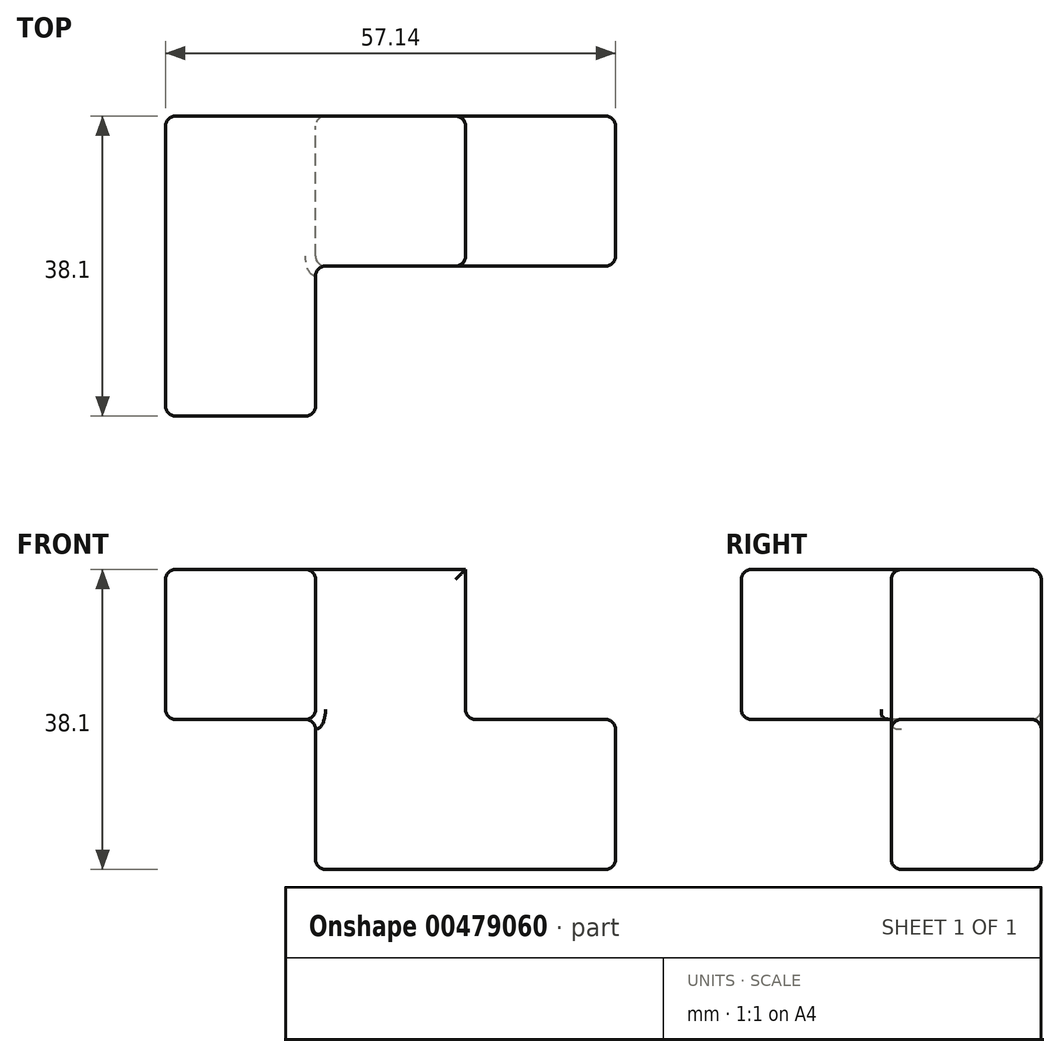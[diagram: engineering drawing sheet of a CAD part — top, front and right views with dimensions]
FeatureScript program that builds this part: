
annotation { "Feature Type Name" : "Feature", "Feature Type Description" : "" }
export const myFeature = defineFeature(function(context is Context, id is Id, definition is map)
    precondition{}
    {
        {
            var Q0;
            Q0=qCreatedBy(makeId("Front.planeOp"),FACE);
            var sketch = newSketch(context, id + "F0", { "sketchPlane" : qUnion([Q0])});
            skLineSegment(sketch, "E0.bottom", {"start": v(-9.53, -19.05) * mm, "end": v(9.52, -19.05) * mm});
            skLineSegment(sketch, "E0.top", {"start": v(-9.52, 19.05) * mm, "end": v(9.53, 19.05) * mm});
            skLineSegment(sketch, "E0.left", {"start": v(-9.53, -19.05) * mm, "end": v(-9.53, 0) * mm});
            skPoint(sketch, "E0.middle", {"position": v(0, 0) * mm});
            skLineSegment(sketch, "E1.bottom", {"start": v(9.52, -19.05) * mm, "end": v(28.57, -19.05) * mm});
            skLineSegment(sketch, "E1.top", {"start": v(9.53, 0) * mm, "end": v(28.57, 0) * mm});
            skLineSegment(sketch, "E1.right", {"start": v(28.57, -19.05) * mm, "end": v(28.57, 0) * mm});
            skPoint(sketch, "E1.middle", {"position": v(19.05, -9.52) * mm});
            skLineSegment(sketch, "E2.trimOffspring", {"start": v(9.53, 0) * mm, "end": v(9.53, 19.05) * mm});
            skLineSegment(sketch, "E3.bottom", {"start": v(9.53, 19.05) * mm, "end": v(-28.57, 19.05) * mm});
            skLineSegment(sketch, "E3.left", {"start": v(9.53, 19.05) * mm, "end": v(9.53, 0) * mm});
            skLineSegment(sketch, "E3.right", {"start": v(-28.57, 19.05) * mm, "end": v(-28.57, 0) * mm});
            skLineSegment(sketch, "E4.trimOffspring", {"start": v(-9.53, 0) * mm, "end": v(-28.57, 0) * mm});
            skSolve(sketch);
        }
        {
            var Q0;
            Q0=makeQuery(id+"F0.imprint","IMPRINT",FACE,{"disambiguationData":[TD([[makeQuery(id+"F0.imprint","IMPRINT",EDGE,{"derivedFrom":sQuery(id+"F0.wireOp",EDGE,"E0.bottom")}),1.0]])]});
            extrude(context, id + "F1", {"entities" : qUnion([Q0]), "endBound" : BoundingType.SYMMETRIC, "depth" : 19.05 * mm});
        }
        {
            var Q0;
            Q0=makeQuery(id+"F1.opExtrude","CAP_FACE",FACE,{"disambiguationData":[OSD([sQuery(id+"F0.wireOp",EDGE,"E0.bottom"),sQuery(id+"F0.wireOp",EDGE,"E0.left"),sQuery(id+"F0.wireOp",EDGE,"E1.bottom"),sQuery(id+"F0.wireOp",EDGE,"E1.top"),sQuery(id+"F0.wireOp",EDGE,"E1.right"),sQuery(id+"F0.wireOp",EDGE,"E3.bottom"),sQuery(id+"F0.wireOp",EDGE,"E3.left"),sQuery(id+"F0.wireOp",EDGE,"E3.right"),sQuery(id+"F0.wireOp",EDGE,"E4.trimOffspring")])],"isStart":false});
            var sketch = newSketch(context, id + "F2", { "sketchPlane" : qUnion([Q0])});
            skLineSegment(sketch, "E5.bottom", {"start": v(-28.57, 19.05) * mm, "end": v(-9.53, 19.05) * mm});
            skLineSegment(sketch, "E5.top", {"start": v(-28.57, 0) * mm, "end": v(-9.53, 0) * mm});
            skLineSegment(sketch, "E5.left", {"start": v(-28.57, 19.05) * mm, "end": v(-28.57, 0) * mm});
            skLineSegment(sketch, "E5.right", {"start": v(-9.53, 19.05) * mm, "end": v(-9.53, 0) * mm});
            skSolve(sketch);
        }
        {
            var Q0;
            Q0 = qSketchRegion(id + "F2", true);
            extrude(context, id + "F3", {"entities" : qUnion([Q0]), "operationType" : NewBodyOperationType.ADD, "depth" : 19.05 * mm});
        }
        {
            var Q0;
            Q0=makeQuery(id+"F1.opExtrude","CAP_FACE",FACE,{"disambiguationData":[OSD([sQuery(id+"F0.wireOp",EDGE,"E0.bottom"),sQuery(id+"F0.wireOp",EDGE,"E0.left"),sQuery(id+"F0.wireOp",EDGE,"E1.bottom"),sQuery(id+"F0.wireOp",EDGE,"E1.top"),sQuery(id+"F0.wireOp",EDGE,"E1.right"),sQuery(id+"F0.wireOp",EDGE,"E3.bottom"),sQuery(id+"F0.wireOp",EDGE,"E3.left"),sQuery(id+"F0.wireOp",EDGE,"E3.right"),sQuery(id+"F0.wireOp",EDGE,"E4.trimOffspring")])],"isStart":true});
            var Q1;
            Q1=makeQuery(id+"F1.opExtrude","SWEPT_FACE",FACE,{"disambiguationData":[OSD([sQuery(id+"F0.wireOp",EDGE,"E0.bottom"),sQuery(id+"F0.wireOp",EDGE,"E1.bottom")])]});
            var Q2;
            Q2=makeQuery(id+"F1.opExtrude","CAP_FACE",FACE,{"disambiguationData":[OSD([sQuery(id+"F0.wireOp",EDGE,"E0.bottom"),sQuery(id+"F0.wireOp",EDGE,"E0.left"),sQuery(id+"F0.wireOp",EDGE,"E1.bottom"),sQuery(id+"F0.wireOp",EDGE,"E1.top"),sQuery(id+"F0.wireOp",EDGE,"E1.right"),sQuery(id+"F0.wireOp",EDGE,"E3.bottom"),sQuery(id+"F0.wireOp",EDGE,"E3.left"),sQuery(id+"F0.wireOp",EDGE,"E3.right"),sQuery(id+"F0.wireOp",EDGE,"E4.trimOffspring")])],"isStart":false});
            var Q3;
            Q3=makeQuery(id+"F1.opExtrude","SWEPT_FACE",FACE,{"disambiguationData":[OSD([sQuery(id+"F0.wireOp",EDGE,"E0.left")])]});
            var Q4;
            Q4=makeQuery(id+"F3.boolean.opBoolean","MERGE",FACE,{"derivedFrom":[makeQuery(id+"F1.opExtrude","SWEPT_FACE",FACE,{"disambiguationData":[OSD([sQuery(id+"F0.wireOp",EDGE,"E4.trimOffspring")])]}),makeQuery(id+"F3.opExtrude","SWEPT_FACE",FACE,{"disambiguationData":[OSD([sQuery(id+"F2.wireOp",EDGE,"E5.top")])]})]});
            var Q5;
            Q5=makeQuery(id+"F3.boolean.opBoolean","MERGE",FACE,{"derivedFrom":[makeQuery(id+"F1.opExtrude","SWEPT_FACE",FACE,{"disambiguationData":[OSD([sQuery(id+"F0.wireOp",EDGE,"E3.right")])]}),makeQuery(id+"F3.opExtrude","SWEPT_FACE",FACE,{"disambiguationData":[OSD([sQuery(id+"F2.wireOp",EDGE,"E5.left")])]})]});
            var Q6;
            Q6=makeQuery(id+"F3.opExtrude","CAP_FACE",FACE,{"disambiguationData":[OSD([sQuery(id+"F2.wireOp",EDGE,"E5.bottom"),sQuery(id+"F2.wireOp",EDGE,"E5.top"),sQuery(id+"F2.wireOp",EDGE,"E5.left"),sQuery(id+"F2.wireOp",EDGE,"E5.right")])],"isStart":false});
            var Q7;
            Q7=makeQuery(id+"F3.opExtrude","SWEPT_FACE",FACE,{"disambiguationData":[OSD([sQuery(id+"F2.wireOp",EDGE,"E5.right")])]});
            var Q8;
            Q8=makeQuery(id+"F1.opExtrude","SWEPT_FACE",FACE,{"disambiguationData":[OSD([sQuery(id+"F0.wireOp",EDGE,"E3.left")])]});
            var Q9;
            Q9=makeQuery(id+"F1.opExtrude","SWEPT_FACE",FACE,{"disambiguationData":[OSD([sQuery(id+"F0.wireOp",EDGE,"E1.top")])]});
            fillet(context, id + "F4", {"entities" : qUnion([Q0, Q1, Q2, Q3, Q4, Q5, Q6, Q7, Q8, Q9]), "radius" : 1.27 * mm, "tangentPropagation" : true, "allowEdgeOverflow" : false});
        }
    });
